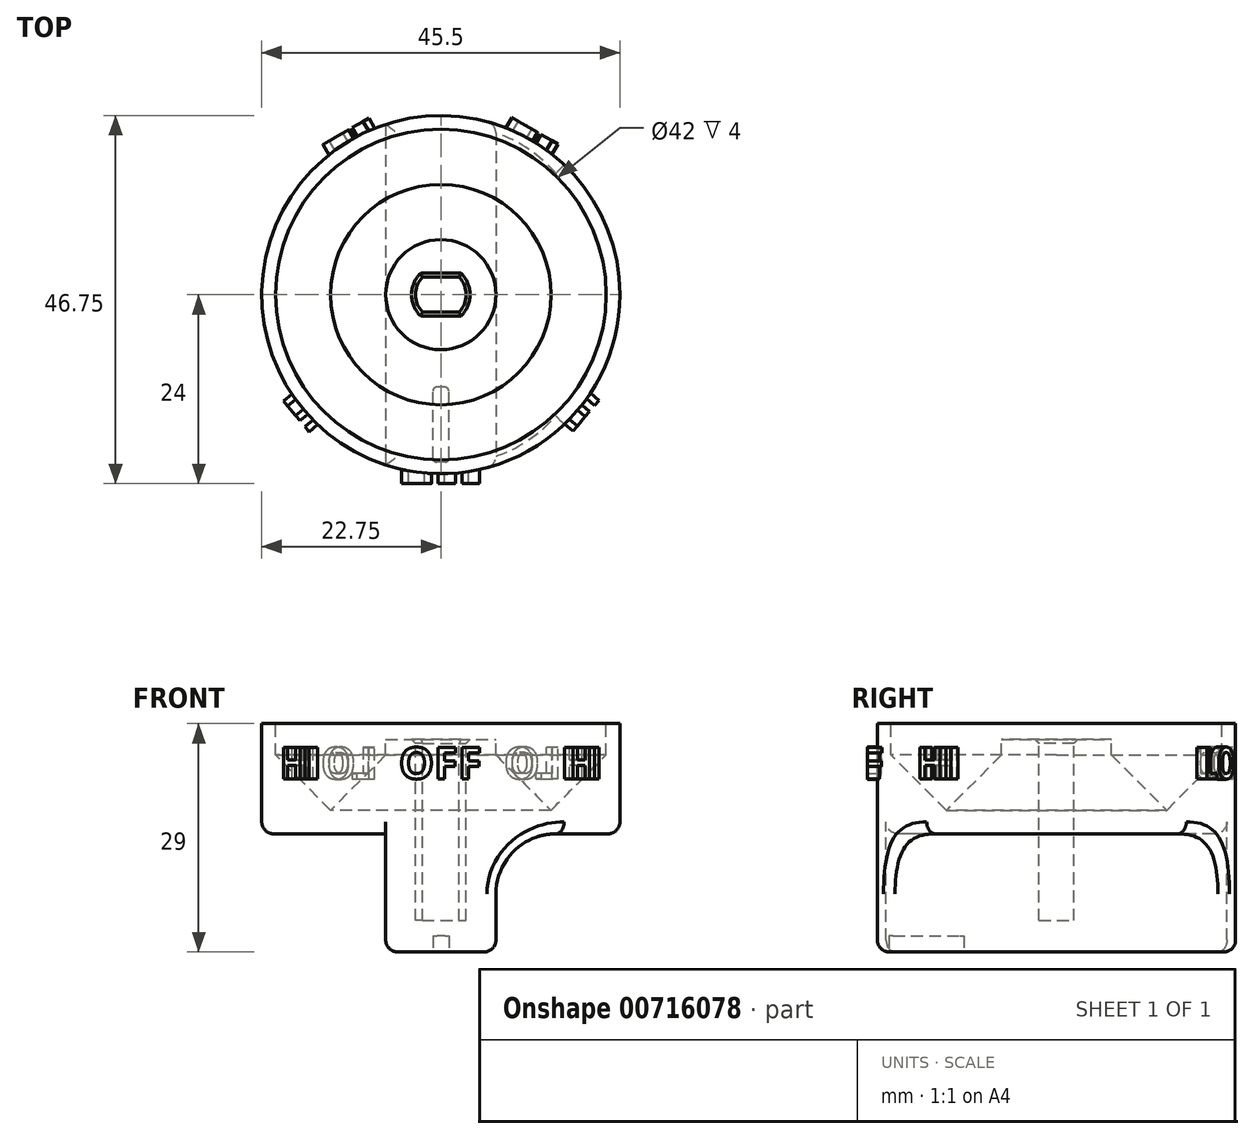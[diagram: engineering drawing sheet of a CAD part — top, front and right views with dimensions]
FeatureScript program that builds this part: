
annotation { "Feature Type Name" : "Feature", "Feature Type Description" : "" }
export const myFeature = defineFeature(function(context is Context, id is Id, definition is map)
    precondition{}
    {
        {
            var Q0;
            Q0=qCreatedBy(makeId("Top.planeOp"),FACE);
            var sketch = newSketch(context, id + "F0", { "sketchPlane" : qUnion([Q0])});
            skCircle(sketch, "E0", {"center": v(0, 0) * mm, "radius": 22.75 * mm});
            skSolve(sketch);
        }
        {
            var Q0;
            Q0=qSketchRegion(id+"F0",true);
            extrude(context, id + "F1", {"entities" : qUnion([Q0]), "depth" : 14 * mm, "offsetDistance" : 25.4 * mm});
        }
        {
            var Q0;
            Q0=makeQuery(id+"F1.opExtrude","CAP_FACE",FACE,{"disambiguationData":[OSD([sQuery(id+"F0.wireOp",EDGE,"E0")])],"isStart":false});
            var sketch = newSketch(context, id + "F2", { "sketchPlane" : qUnion([Q0])});
            skLineSegment(sketch, "E1.left", {"start": v(-7, 21.65) * mm, "end": v(-7, -21.65) * mm});
            skLineSegment(sketch, "E1.right", {"start": v(7, 21.65) * mm, "end": v(7, -21.65) * mm});
            skPoint(sketch, "E2", {"position": v(0, 24.49) * mm});
            skLineSegment(sketch, "E3", {"start": v(0, 34.26) * mm, "end": v(0, -28.44) * mm, "construction": true});
            skLineSegment(sketch, "E4", {"start": v(19.58, 0) * mm, "end": v(-22.13, 0) * mm, "construction": true});
            skArc(sketch, "E5.0", {"start": v(-7, -21.65) * mm, "mid": v(0, -22.75) * mm, "end": v(7, -21.65) * mm});
            skArc(sketch, "E6.trimOffspring", {"start": v(7, 21.65) * mm, "mid": v(0, 22.75) * mm, "end": v(-7, 21.65) * mm});
            skPoint(sketch, "E7.orphan", {"position": v(-7, 24.49) * mm});
            skPoint(sketch, "E1.bottom.end.orphan", {"position": v(7, 24.49) * mm});
            skPoint(sketch, "E8.orphan", {"position": v(7, -23.15) * mm});
            skSolve(sketch);
        }
        {
            var Q0;
            Q0=qSketchRegion(id+"F2",true);
            extrude(context, id + "F3", {"entities" : qUnion([Q0]), "operationType" : NewBodyOperationType.ADD, "depth" : 15 * mm, "offsetDistance" : 25 * mm});
        }
        {
            var Q0;
            Q0=makeQuery(id+"F3.opExtrude","CAP_FACE",FACE,{"disambiguationData":[OSD([sQuery(id+"F2.wireOp",EDGE,"E1.left"),sQuery(id+"F2.wireOp",EDGE,"E1.right"),sQuery(id+"F2.wireOp",EDGE,"E5.0"),sQuery(id+"F2.wireOp",EDGE,"E6.trimOffspring")])],"isStart":false});
            var sketch = newSketch(context, id + "F4", { "sketchPlane" : qUnion([Q0])});
            skLineSegment(sketch, "E9.bottom", {"start": v(0.5, -21.28) * mm, "end": v(-0.5, -21.28) * mm});
            skLineSegment(sketch, "E9.top", {"start": v(0.5, -11.75) * mm, "end": v(-0.5, -11.75) * mm});
            skLineSegment(sketch, "E9.left", {"start": v(1.02, -20.77) * mm, "end": v(1.02, -12.26) * mm});
            skLineSegment(sketch, "E9.right", {"start": v(-1.02, -20.77) * mm, "end": v(-1.02, -12.26) * mm});
            skPoint(sketch, "E10", {"position": v(0, -21.28) * mm});
            skLineSegment(sketch, "E11", {"start": v(0, -16.34) * mm, "end": v(0, 0) * mm, "construction": true});
            skPoint(sketch, "E12.visualSharp", {"position": v(1.02, -21.28) * mm});
            skArc(sketch, "E12.filletArc", {"start": v(0.5, -21.28) * mm, "mid": v(0.87, -21.13) * mm, "end": v(1.02, -20.77) * mm});
            skPoint(sketch, "E13.visualSharp", {"position": v(-1.02, -21.28) * mm});
            skArc(sketch, "E13.filletArc", {"start": v(-1.02, -20.77) * mm, "mid": v(-0.87, -21.13) * mm, "end": v(-0.5, -21.28) * mm});
            skPoint(sketch, "E14.visualSharp", {"position": v(-1.02, -11.75) * mm});
            skArc(sketch, "E14.filletArc", {"start": v(-0.5, -11.75) * mm, "mid": v(-0.87, -11.9) * mm, "end": v(-1.02, -12.26) * mm});
            skPoint(sketch, "E15.visualSharp", {"position": v(1.02, -11.75) * mm});
            skArc(sketch, "E15.filletArc", {"start": v(1.02, -12.26) * mm, "mid": v(0.87, -11.9) * mm, "end": v(0.5, -11.75) * mm});
            skSolve(sketch);
        }
        {
            var Q0;
            Q0=makeQuery(id+"F3.opExtrude","CAP_EDGE",EDGE,{"disambiguationData":[OSD([sQuery(id+"F2.wireOp",EDGE,"E1.left")])],"isStart":true});
            var Q1;
            Q1=makeQuery(id+"F3.opExtrude","CAP_EDGE",EDGE,{"disambiguationData":[OSD([sQuery(id+"F2.wireOp",EDGE,"E1.right")])],"isStart":true});
            fillet(context, id + "F5", {"entities" : qUnion([Q0, Q1]), "radius" : 7.62 * mm, "tangentPropagation" : true, "allowEdgeOverflow" : false});
        }
        {
            var Q0;
            {var subQ0=sQuery(id+"F0.wireOp",EDGE,"E0");Q0=makeQuery(id+"F3.boolean.opBoolean","SPLIT",EDGE,{"disambiguationData":[TD([makeQuery(id+"F3.opExtrude","SWEPT_FACE",FACE,{"disambiguationData":[OSD([sQuery(id+"F2.wireOp",EDGE,"E1.left")])]})])],"derivedFrom":makeQuery(id+"F1.opExtrude","CAP_EDGE",EDGE,{"disambiguationData":[OSD([subQ0])],"isStart":false})});}
            var Q1;
            {var subQ0=sQuery(id+"F0.wireOp",EDGE,"E0");Q1=makeQuery(id+"F3.boolean.opBoolean","SPLIT",EDGE,{"disambiguationData":[TD([makeQuery(id+"F3.opExtrude","SWEPT_FACE",FACE,{"disambiguationData":[OSD([sQuery(id+"F2.wireOp",EDGE,"E1.right")])]})])],"derivedFrom":makeQuery(id+"F1.opExtrude","CAP_EDGE",EDGE,{"disambiguationData":[OSD([subQ0])],"isStart":false})});}
            var Q2;
            Q2=makeQuery(id+"F3.opExtrude","CAP_EDGE",EDGE,{"disambiguationData":[OSD([sQuery(id+"F2.wireOp",EDGE,"E5.0")])],"isStart":false});
            var Q3;
            Q3=makeQuery(id+"F3.opExtrude","CAP_EDGE",EDGE,{"disambiguationData":[OSD([sQuery(id+"F2.wireOp",EDGE,"E1.left")])],"isStart":false});
            var Q4;
            Q4=makeQuery(id+"F3.opExtrude","CAP_EDGE",EDGE,{"disambiguationData":[OSD([sQuery(id+"F2.wireOp",EDGE,"E1.right")])],"isStart":false});
            var Q5;
            Q5=makeQuery(id+"F3.opExtrude","CAP_EDGE",EDGE,{"disambiguationData":[OSD([sQuery(id+"F2.wireOp",EDGE,"E6.trimOffspring")])],"isStart":false});
            fillet(context, id + "F6", {"entities" : qUnion([Q0, Q1, Q2, Q3, Q4, Q5]), "radius" : 1.52 * mm, "tangentPropagation" : true, "allowEdgeOverflow" : false});
        }
        {
            var Q0;
            Q0=makeQuery(id+"F1.opExtrude","CAP_FACE",FACE,{"disambiguationData":[OSD([sQuery(id+"F0.wireOp",EDGE,"E0")])],"isStart":true});
            var sketch = newSketch(context, id + "F7", { "sketchPlane" : qUnion([Q0])});
            skCircle(sketch, "E16", {"center": v(0, 0) * mm, "radius": 3.22 * mm});
            skLineSegment(sketch, "E17.bottom", {"start": v(-2.33, -2.22) * mm, "end": v(2.33, -2.22) * mm});
            skLineSegment(sketch, "E17.top", {"start": v(-2.33, 2.22) * mm, "end": v(2.33, 2.22) * mm});
            skLineSegment(sketch, "E17.left", {"start": v(-2.33, -2.22) * mm, "end": v(-2.33, 2.22) * mm});
            skLineSegment(sketch, "E17.right", {"start": v(2.33, -2.22) * mm, "end": v(2.33, 2.22) * mm});
            skSolve(sketch);
        }
        {
            var Q0;
            Q0=makeQuery(id+"F7.imprint","IMPRINT",FACE,{"disambiguationData":[TD([[makeQuery(id+"F7.imprint","IMPRINT",EDGE,{"derivedFrom":sQuery(id+"F7.wireOp",EDGE,"E17.bottom")}),1.0]])]});
            var Q1;
            {var subQ0=sQuery(id+"F7.wireOp",EDGE,"E17.left");Q1=makeQuery(id+"F7.imprint","IMPRINT",FACE,{"disambiguationData":[TD([[makeQuery(id+"F7.imprint","IMPRINT",EDGE,{"derivedFrom":subQ0}),1.0]])]});}
            var Q2;
            {var subQ0=sQuery(id+"F7.wireOp",EDGE,"E17.right");Q2=makeQuery(id+"F7.imprint","IMPRINT",FACE,{"disambiguationData":[TD([[makeQuery(id+"F7.imprint","IMPRINT",EDGE,{"derivedFrom":subQ0}),-1.0]])]});}
            extrude(context, id + "F8", {"entities" : qUnion([Q0, Q1, Q2]), "operationType" : NewBodyOperationType.REMOVE, "depth" : 15.24 * mm, "offsetDistance" : 25.4 * mm});
        }
        {
            var Q0;
            Q0=qSketchRegion(id+"F4",true);
            extrude(context, id + "F9", {"entities" : qUnion([Q0]), "operationType" : NewBodyOperationType.REMOVE, "oppositeDirection" : true, "depth" : 2.03 * mm});
        }
        {
            var Q0;
            Q0=makeQuery(id+"F1.opExtrude","CAP_FACE",FACE,{"disambiguationData":[OSD([sQuery(id+"F0.wireOp",EDGE,"E0")])],"isStart":true});
            var sketch = newSketch(context, id + "F10", { "sketchPlane" : qUnion([Q0])});
            skCircle(sketch, "E18", {"center": v(0, 0) * mm, "radius": 7.94 * mm});
            skSolve(sketch);
        }
        {
            var Q0;
            Q0=qSketchRegion(id+"F10",true);
            extrude(context, id + "F11", {"entities" : qUnion([Q0]), "operationType" : NewBodyOperationType.REMOVE, "oppositeDirection" : true, "depth" : 2 * mm, "offsetDistance" : 25 * mm});
        }
        {
            var Q0;
            Q0=makeQuery(id+"F1.opExtrude","CAP_FACE",FACE,{"disambiguationData":[OSD([sQuery(id+"F0.wireOp",EDGE,"E0")])],"isStart":true});
            var sketch = newSketch(context, id + "F12", { "sketchPlane" : qUnion([Q0])});
            skCircle(sketch, "E19", {"center": v(0, 0) * mm, "radius": 21 * mm});
            skCircle(sketch, "E20", {"center": v(0, 0) * mm, "radius": 7 * mm});
            skSolve(sketch);
        }
        {
            var Q0;
            Q0=qSketchRegion(id+"F12",true);
            extrude(context, id + "F13", {"entities" : qUnion([Q0]), "operationType" : NewBodyOperationType.REMOVE, "oppositeDirection" : true, "depth" : 11 * mm, "offsetDistance" : 25 * mm});
        }
        {
            var Q0;
            Q0=qCreatedBy(makeId("Top.planeOp"),FACE);
            cPlane(context, id + "F14", {"entities" : qUnion([Q0]), "cplaneType" : CPlaneType.OFFSET, "offset" : 0 * mm, "width" : 150 * mm, "height" : 150 * mm});
        }
        {
            var Q0;
            Q0=makeQuery(id+"F1.opExtrude","SWEPT_BODY",BODY,{"disambiguationData":[OSD([sQuery(id+"F0.wireOp",EDGE,"E0")])]});
            var Q1;
            Q1=qCreatedBy(id+"F14.planeOp",FACE);
            mirror(context, id + "F15", {"entities" : qUnion([Q0]), "mirrorPlane" : qUnion([Q1])});
        }
        {
            var Q0;
            Q0=qCreatedBy(makeId("Front.planeOp"),FACE);
            var sketch = newSketch(context, id + "F16", { "sketchPlane" : qUnion([Q0])});
            skLineSegment(sketch, "E21", {"start": v(0, 0) * mm, "end": v(0, -63.03) * mm});
            skSolve(sketch);
        }
        {
            var Q0;
            Q0=sQuery(id+"F16.wireOp",EDGE,"E21");
            cPlane(context, id + "F17", {"entities" : qUnion([Q0]), "cplaneType" : CPlaneType.LINE_ANGLE, "offset" : 25 * mm, "angle" : 40 * degree, "oppositeDirection" : true, "width" : 150 * mm, "height" : 150 * mm});
        }
        {
            var Q0;
            Q0=qCreatedBy(id+"F17.planeOp",FACE);
            var sketch = newSketch(context, id + "F18", { "sketchPlane" : qUnion([Q0])});
            skText(sketch, "E22", { "text": "HI", "fontName": "OpenSans-Bold.ttf"});
            const initialGuessF18  = {"E22": [-0.00298, -0.007, 1, 0, 0.004]};
            skSetInitialGuess(sketch, initialGuessF18);
            skSolve(sketch);
        }
        {
            var Q0;
            Q0 = qSketchRegion(id + "F18", true);
            extrude(context, id + "F19", {"entities" : qUnion([Q0]), "operationType" : NewBodyOperationType.ADD, "depth" : 24 * mm, "offsetDistance" : 25 * mm, "hasSecondDirection" : true, "secondDirectionOppositeDirection" : false, "secondDirectionDepth" : 22 * mm});
        }
        {
            var Q0;
            Q0=sQuery(id+"F16.wireOp",EDGE,"E21");
            cPlane(context, id + "F20", {"entities" : qUnion([Q0]), "cplaneType" : CPlaneType.LINE_ANGLE, "offset" : 25 * mm, "angle" : 270 * degree, "width" : 150 * mm, "height" : 150 * mm});
        }
        {
            var Q0;
            Q0=qCreatedBy(id+"F20.planeOp",FACE);
            var sketch = newSketch(context, id + "F21", { "sketchPlane" : qUnion([Q0])});
            skText(sketch, "E23", { "text": "OFF", "fontName": "OpenSans-Bold.ttf"});
            const initialGuessF21  = {"E23": [-0.0053, -0.007, 1, 0, 0.004]};
            skSetInitialGuess(sketch, initialGuessF21);
            skSolve(sketch);
        }
        {
            var Q0;
            Q0 = qSketchRegion(id + "F21", true);
            extrude(context, id + "F22", {"entities" : qUnion([Q0]), "operationType" : NewBodyOperationType.ADD, "depth" : 24 * mm, "offsetDistance" : 25 * mm, "hasSecondDirection" : true, "secondDirectionOppositeDirection" : false, "secondDirectionDepth" : 22 * mm});
        }
        {
            var Q0;
            Q0=qCreatedBy(makeId("Front.planeOp"),FACE);
            var sketch = newSketch(context, id + "F23", { "sketchPlane" : qUnion([Q0])});
            skLineSegment(sketch, "E24", {"start": v(0, 0) * mm, "end": v(0, -52.58) * mm, "construction": true});
            skSolve(sketch);
        }
        {
            var Q0;
            Q0=sQuery(id+"F23.wireOp",EDGE,"E24");
            cPlane(context, id + "F24", {"entities" : qUnion([Q0]), "cplaneType" : CPlaneType.LINE_ANGLE, "offset" : 25 * mm, "angle" : 140 * degree, "oppositeDirection" : true, "width" : 150 * mm, "height" : 150 * mm});
        }
        {
            var Q0;
            Q0=qCreatedBy(id+"F24.planeOp",FACE);
            var sketch = newSketch(context, id + "F25", { "sketchPlane" : qUnion([Q0])});
            skText(sketch, "E25", { "text": "HI", "fontName": "OpenSans-Bold.ttf"});
            const initialGuessF25  = {"E25": [-0.00298, -0.007, 1, 0, 0.004]};
            skSetInitialGuess(sketch, initialGuessF25);
            skSolve(sketch);
        }
        {
            var Q0;
            Q0 = qSketchRegion(id + "F25", true);
            extrude(context, id + "F26", {"entities" : qUnion([Q0]), "operationType" : NewBodyOperationType.ADD, "depth" : 24 * mm, "offsetDistance" : 25 * mm, "hasSecondDirection" : true, "secondDirectionOppositeDirection" : false, "secondDirectionDepth" : 22 * mm});
        }
        {
            var Q0;
            Q0=sQuery(id+"F23.wireOp",EDGE,"E24");
            cPlane(context, id + "F27", {"entities" : qUnion([Q0]), "cplaneType" : CPlaneType.LINE_ANGLE, "offset" : 25 * mm, "angle" : 60 * degree, "width" : 150 * mm, "height" : 150 * mm});
        }
        {
            var Q0;
            Q0=qCreatedBy(id+"F27.planeOp",FACE);
            var sketch = newSketch(context, id + "F28", { "sketchPlane" : qUnion([Q0])});
            skText(sketch, "E26", { "text": "LO", "fontName": "OpenSans-Bold.ttf"});
            const initialGuessF28  = {"E26": [-0.0038, -0.007, 1, 0, 0.004]};
            skSetInitialGuess(sketch, initialGuessF28);
            skSolve(sketch);
        }
        {
            var Q0;
            Q0 = qSketchRegion(id + "F28", true);
            extrude(context, id + "F29", {"entities" : qUnion([Q0]), "operationType" : NewBodyOperationType.ADD, "depth" : 24 * mm, "offsetDistance" : 25 * mm, "hasSecondDirection" : true, "secondDirectionOppositeDirection" : false, "secondDirectionDepth" : 22 * mm});
        }
        {
            var Q0;
            Q0=sQuery(id+"F23.wireOp",EDGE,"E24");
            cPlane(context, id + "F30", {"entities" : qUnion([Q0]), "cplaneType" : CPlaneType.LINE_ANGLE, "offset" : 25 * mm, "angle" : 120 * degree, "width" : 150 * mm, "height" : 150 * mm});
        }
        {
            var Q0;
            Q0=qCreatedBy(id+"F30.planeOp",FACE);
            var sketch = newSketch(context, id + "F31", { "sketchPlane" : qUnion([Q0])});
            skText(sketch, "E27", { "text": "LO", "fontName": "OpenSans-Bold.ttf"});
            const initialGuessF31  = {"E27": [-0.0038, -0.007, 1, 0, 0.004]};
            skSetInitialGuess(sketch, initialGuessF31);
            skSolve(sketch);
        }
        {
            var Q0;
            Q0 = qSketchRegion(id + "F31", true);
            extrude(context, id + "F32", {"entities" : qUnion([Q0]), "operationType" : NewBodyOperationType.ADD, "depth" : 24 * mm, "offsetDistance" : 25 * mm, "hasSecondDirection" : true, "secondDirectionOppositeDirection" : false, "secondDirectionDepth" : 22 * mm});
        }
        {
            var Q0;
            Q0=makeQuery(id+"F7.imprint","IMPRINT",FACE,{"disambiguationData":[TD([[makeQuery(id+"F7.imprint","IMPRINT",EDGE,{"derivedFrom":sQuery(id+"F7.wireOp",EDGE,"E17.bottom")}),1.0]])]});
            var Q1;
            {var subQ0=sQuery(id+"F7.wireOp",EDGE,"E17.right");Q1=makeQuery(id+"F7.imprint","IMPRINT",FACE,{"disambiguationData":[TD([[makeQuery(id+"F7.imprint","IMPRINT",EDGE,{"derivedFrom":subQ0}),-1.0]])]});}
            var Q2;
            {var subQ0=sQuery(id+"F7.wireOp",EDGE,"E17.left");Q2=makeQuery(id+"F7.imprint","IMPRINT",FACE,{"disambiguationData":[TD([[makeQuery(id+"F7.imprint","IMPRINT",EDGE,{"derivedFrom":subQ0}),1.0]])]});}
            extrude(context, id + "F33", {"entities" : qUnion([Q0, Q1, Q2]), "operationType" : NewBodyOperationType.REMOVE, "depth" : 25 * mm, "offsetDistance" : 25 * mm});
        }
        {
            var Q0;
            Q0=makeQuery(id+"F1.opExtrude","SWEPT_BODY",BODY,{"disambiguationData":[OSD([sQuery(id+"F0.wireOp",EDGE,"E0")])]});
            deleteBodies(context, id + "F34", {"entities" : qUnion([Q0])});
        }
        {
            var Q0;
            Q0=makeQuery(id+"F33.boolean.opBoolean","INTERSECT",EDGE,{"derivedFrom":[makeQuery(id+"F15.opPattern","COPY",FACE,{"derivedFrom":makeQuery(id+"F11.boolean.opBoolean","COPY",FACE,{"derivedFrom":makeQuery(id+"F11.opExtrude","CAP_FACE",FACE,{"disambiguationData":[OSD([sQuery(id+"F10.wireOp",EDGE,"E18")])],"isStart":false})}),"instanceName":"1"}),makeQuery(id+"F33.opExtrude","SWEPT_FACE",FACE,{"disambiguationData":[OSD([sQuery(id+"F7.wireOp",EDGE,"E17.top")])]})]});
            var Q1;
            Q1=makeQuery(id+"F33.boolean.opBoolean","INTERSECT",EDGE,{"derivedFrom":[makeQuery(id+"F15.opPattern","COPY",FACE,{"derivedFrom":makeQuery(id+"F11.boolean.opBoolean","COPY",FACE,{"derivedFrom":makeQuery(id+"F11.opExtrude","CAP_FACE",FACE,{"disambiguationData":[OSD([sQuery(id+"F10.wireOp",EDGE,"E18")])],"isStart":false})}),"instanceName":"1"}),makeQuery(id+"F33.opExtrude","SWEPT_FACE",FACE,{"disambiguationData":[OSD([sQuery(id+"F7.wireOp",EDGE,"E17.bottom")])]})]});
            var Q2;
            {var subQ0=sQuery(id+"F7.wireOp",EDGE,"E17.right");var subQ1=sQuery(id+"F7.wireOp",EDGE,"E16");Q2=makeQuery(id+"F33.boolean.opBoolean","INTERSECT",EDGE,{"derivedFrom":[makeQuery(id+"F15.opPattern","COPY",FACE,{"derivedFrom":makeQuery(id+"F11.boolean.opBoolean","COPY",FACE,{"derivedFrom":makeQuery(id+"F11.opExtrude","CAP_FACE",FACE,{"disambiguationData":[OSD([sQuery(id+"F10.wireOp",EDGE,"E18")])],"isStart":false})}),"instanceName":"1"}),makeQuery(id+"F33.opExtrude","SWEPT_FACE",FACE,{"disambiguationData":[OSD([subQ1]),TDD([makeQuery(id+"F7.imprint","IMPRINT",EDGE,{"disambiguationData":[TD([[makeQuery(id+"F7.imprint","INTERSECT",VERTEX,{"derivedFrom":[subQ1,sQuery(id+"F7.wireOp",EDGE,"E17.bottom"),subQ0]}),-1.0]])],"derivedFrom":subQ1})])]})]});}
            var Q3;
            {var subQ0=sQuery(id+"F7.wireOp",EDGE,"E17.left");var subQ1=sQuery(id+"F7.wireOp",EDGE,"E16");Q3=makeQuery(id+"F33.boolean.opBoolean","INTERSECT",EDGE,{"derivedFrom":[makeQuery(id+"F15.opPattern","COPY",FACE,{"derivedFrom":makeQuery(id+"F11.boolean.opBoolean","COPY",FACE,{"derivedFrom":makeQuery(id+"F11.opExtrude","CAP_FACE",FACE,{"disambiguationData":[OSD([sQuery(id+"F10.wireOp",EDGE,"E18")])],"isStart":false})}),"instanceName":"1"}),makeQuery(id+"F33.opExtrude","SWEPT_FACE",FACE,{"disambiguationData":[OSD([subQ1]),TDD([makeQuery(id+"F7.imprint","IMPRINT",EDGE,{"disambiguationData":[TD([[makeQuery(id+"F7.imprint","INTERSECT",VERTEX,{"derivedFrom":[subQ1,sQuery(id+"F7.wireOp",EDGE,"E17.bottom"),subQ0]}),1.0]])],"derivedFrom":subQ1})])]})]});}
            chamfer(context, id + "F35", {"entities" : qUnion([Q0, Q1, Q2, Q3]), "width" : 0.5 * mm, "tangentPropagation" : true});
        }
        {
            var Q0;
            Q0=makeQuery(id+"F15.opPattern","COPY",EDGE,{"derivedFrom":makeQuery(id+"F13.boolean.opBoolean","COPY",EDGE,{"derivedFrom":makeQuery(id+"F13.opExtrude","CAP_EDGE",EDGE,{"disambiguationData":[OSD([sQuery(id+"F12.wireOp",EDGE,"E19")])],"isStart":false})}),"instanceName":"1"});
            var Q1;
            Q1=makeQuery(id+"F15.opPattern","COPY",EDGE,{"derivedFrom":makeQuery(id+"F13.boolean.opBoolean","COPY",EDGE,{"derivedFrom":makeQuery(id+"F13.opExtrude","CAP_EDGE",EDGE,{"disambiguationData":[OSD([sQuery(id+"F12.wireOp",EDGE,"E20")])],"isStart":false})}),"instanceName":"1"});
            chamfer(context, id + "F36", {"entities" : qUnion([Q0, Q1]), "width" : 7 * mm, "tangentPropagation" : true});
        }
    });
